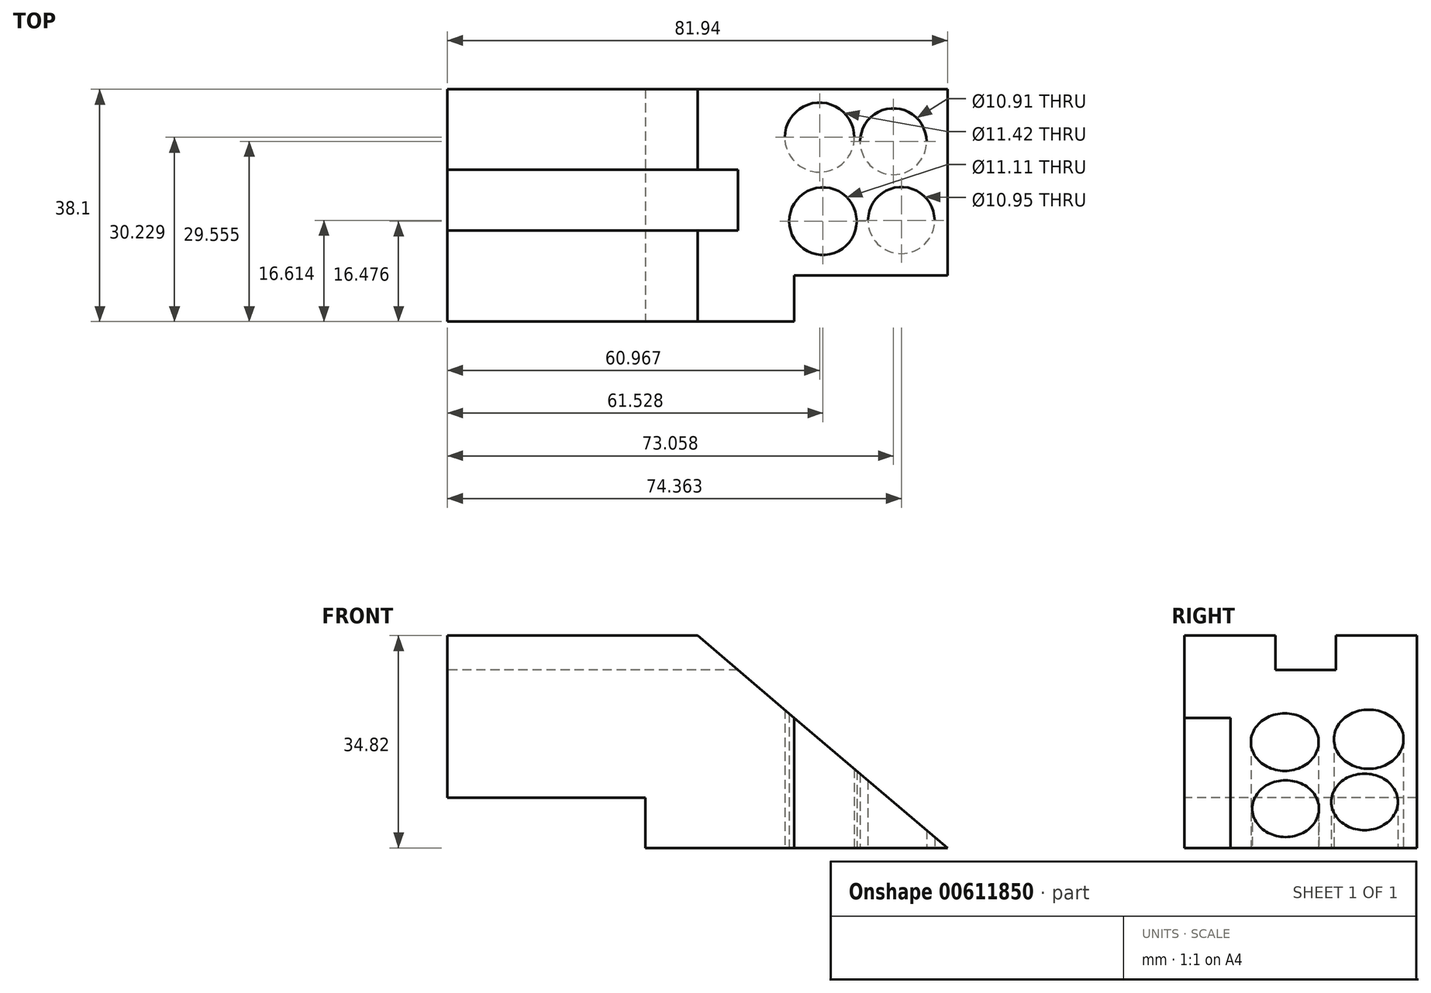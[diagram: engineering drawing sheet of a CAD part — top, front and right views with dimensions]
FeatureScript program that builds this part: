
annotation { "Feature Type Name" : "Feature", "Feature Type Description" : "" }
export const myFeature = defineFeature(function(context is Context, id is Id, definition is map)
    precondition{}
    {
        {
            var Q0;
            Q0=qCreatedBy(makeId("Front.planeOp"),FACE);
            var sketch = newSketch(context, id + "F0", { "sketchPlane" : qUnion([Q0])});
            skLineSegment(sketch, "E0.bottom", {"start": v(-40.97, 17.41) * mm, "end": v(0, 17.41) * mm});
            skLineSegment(sketch, "E0.top", {"start": v(-8.52, -17.41) * mm, "end": v(40.97, -17.41) * mm});
            skLineSegment(sketch, "E0.left", {"start": v(-40.97, 17.41) * mm, "end": v(-40.97, -9.16) * mm});
            skPoint(sketch, "E0.middle", {"position": v(0, 0) * mm});
            skLineSegment(sketch, "E1.top", {"start": v(-40.97, -9.16) * mm, "end": v(-8.52, -9.16) * mm});
            skLineSegment(sketch, "E1.right", {"start": v(-8.52, -17.41) * mm, "end": v(-8.52, -9.16) * mm});
            skPoint(sketch, "E2.orphan", {"position": v(-40.97, -17.41) * mm});
            skLineSegment(sketch, "E3", {"start": v(40.97, -17.41) * mm, "end": v(0, 17.41) * mm});
            skPoint(sketch, "E0.right.start.orphan", {"position": v(40.97, 17.41) * mm});
            skSolve(sketch);
        }
        {
            var Q0;
            Q0=makeQuery(id+"F0.imprint","IMPRINT",FACE,{"disambiguationData":[TD([[makeQuery(id+"F0.imprint","IMPRINT",EDGE,{"derivedFrom":sQuery(id+"F0.wireOp",EDGE,"E0.bottom")}),-1.0]])]});
            extrude(context, id + "F1", {"entities" : qUnion([Q0]), "oppositeDirection" : true, "depth" : 38.1 * mm, "offsetDistance" : 25.4 * mm});
        }
        {
            var Q0;
            Q0=makeQuery(id+"F1.opExtrude","SWEPT_FACE",FACE,{"disambiguationData":[OSD([sQuery(id+"F0.wireOp",EDGE,"E0.top")])]});
            var sketch = newSketch(context, id + "F2", { "sketchPlane" : qUnion([Q0])});
            skLineSegment(sketch, "E4.bottom", {"start": v(40.97, 0) * mm, "end": v(15.86, 0) * mm});
            skLineSegment(sketch, "E4.top", {"start": v(40.97, -7.58) * mm, "end": v(15.86, -7.58) * mm});
            skLineSegment(sketch, "E4.left", {"start": v(40.97, 0) * mm, "end": v(40.97, -7.58) * mm});
            skLineSegment(sketch, "E4.right", {"start": v(15.86, 0) * mm, "end": v(15.86, -7.58) * mm});
            skSolve(sketch);
        }
        {
            var Q0;
            Q0=makeQuery(id+"F2.imprint","IMPRINT",FACE,{"disambiguationData":[TD([[makeQuery(id+"F2.imprint","IMPRINT",EDGE,{"derivedFrom":sQuery(id+"F2.wireOp",EDGE,"E4.bottom")}),-1.0]])]});
            extrude(context, id + "F3", {"entities" : qUnion([Q0]), "operationType" : NewBodyOperationType.REMOVE, "oppositeDirection" : true, "depth" : 25.4 * mm, "offsetDistance" : 25.4 * mm});
        }
        {
            var Q0;
            Q0=makeQuery(id+"F1.opExtrude","SWEPT_FACE",FACE,{"disambiguationData":[OSD([sQuery(id+"F0.wireOp",EDGE,"E0.left")])]});
            var sketch = newSketch(context, id + "F4", { "sketchPlane" : qUnion([Q0])});
            skLineSegment(sketch, "E5.bottom", {"start": v(-24.88, 17.41) * mm, "end": v(-14.94, 17.41) * mm});
            skLineSegment(sketch, "E5.top", {"start": v(-24.88, 11.76) * mm, "end": v(-14.94, 11.76) * mm});
            skLineSegment(sketch, "E5.left", {"start": v(-24.88, 17.41) * mm, "end": v(-24.88, 11.76) * mm});
            skLineSegment(sketch, "E5.right", {"start": v(-14.94, 17.41) * mm, "end": v(-14.94, 11.76) * mm});
            skSolve(sketch);
        }
        {
            var Q0;
            Q0=makeQuery(id+"F4.imprint","IMPRINT",FACE,{"disambiguationData":[TD([[makeQuery(id+"F4.imprint","IMPRINT",EDGE,{"derivedFrom":sQuery(id+"F4.wireOp",EDGE,"E5.bottom")}),-1.0]])]});
            extrude(context, id + "F5", {"entities" : qUnion([Q0]), "operationType" : NewBodyOperationType.REMOVE, "oppositeDirection" : true, "depth" : 228.6 * mm, "offsetDistance" : 25.4 * mm});
        }
        {
            var Q0;
            Q0=makeQuery(id+"F1.opExtrude","SWEPT_FACE",FACE,{"disambiguationData":[OSD([sQuery(id+"F0.wireOp",EDGE,"E0.top")])]});
            var sketch = newSketch(context, id + "F6", { "sketchPlane" : qUnion([Q0])});
            skCircle(sketch, "E6", {"center": v(32.09, -29.55) * mm, "radius": 5.46 * mm});
            skCircle(sketch, "E7", {"center": v(33.4, -16.61) * mm, "radius": 5.48 * mm});
            skCircle(sketch, "E8", {"center": v(20, -30.23) * mm, "radius": 5.7 * mm});
            skCircle(sketch, "E9", {"center": v(20.56, -16.48) * mm, "radius": 5.56 * mm});
            skSolve(sketch);
        }
        {
            var Q0;
            Q0=makeQuery(id+"F6.imprint","IMPRINT",FACE,{"disambiguationData":[TD([[makeQuery(id+"F6.imprint","IMPRINT",EDGE,{"derivedFrom":sQuery(id+"F6.wireOp",EDGE,"E6")}),1.0]])]});
            var Q1;
            Q1=makeQuery(id+"F6.imprint","IMPRINT",FACE,{"disambiguationData":[TD([[makeQuery(id+"F6.imprint","IMPRINT",EDGE,{"derivedFrom":sQuery(id+"F6.wireOp",EDGE,"E8")}),1.0]])]});
            var Q2;
            Q2=makeQuery(id+"F6.imprint","IMPRINT",FACE,{"disambiguationData":[TD([[makeQuery(id+"F6.imprint","IMPRINT",EDGE,{"derivedFrom":sQuery(id+"F6.wireOp",EDGE,"E9")}),1.0]])]});
            var Q3;
            Q3=makeQuery(id+"F6.imprint","IMPRINT",FACE,{"disambiguationData":[TD([[makeQuery(id+"F6.imprint","IMPRINT",EDGE,{"derivedFrom":sQuery(id+"F6.wireOp",EDGE,"E7")}),1.0]])]});
            extrude(context, id + "F7", {"entities" : qUnion([Q0, Q1, Q2, Q3]), "operationType" : NewBodyOperationType.REMOVE, "oppositeDirection" : true, "depth" : 101.6 * mm, "offsetDistance" : 25.4 * mm});
        }
    });
